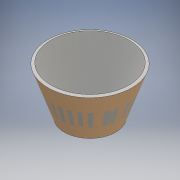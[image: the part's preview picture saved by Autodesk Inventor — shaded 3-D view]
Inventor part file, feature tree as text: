
AUTODESK INVENTOR PART (.ipt)
format: ipt  version: 2016 (Build 200138000, 138)  size: 117,248 bytes
history: native  units: mm
features: sketch x2, plane x1, thicken_offset x1, other x1, loft x1
ambient origin geometry x8: Origin, YZ Plane, XZ Plane, XY Plane, X Axis, Y Axis, Z Axis, Center Point
bodies: Body1 (feature_tree), Body2 (feature_tree)
feature tree (6):
  sketch  "Sketch1"  dims[d0=273.0mm d1=9.52mm]
  plane  "Work Plane1"
  thicken_offset  "Thicken1"
  sketch  "Sketch2"  dims[d2=-152.0mm d3=168.0mm d4=9.52mm d15=0.0mm d16=90.0deg d17=0.0mm d18=90.0deg d19=9.52mm d20=9.52mm]
  other  "Srf1"
  loft  "LoftSrf1"
